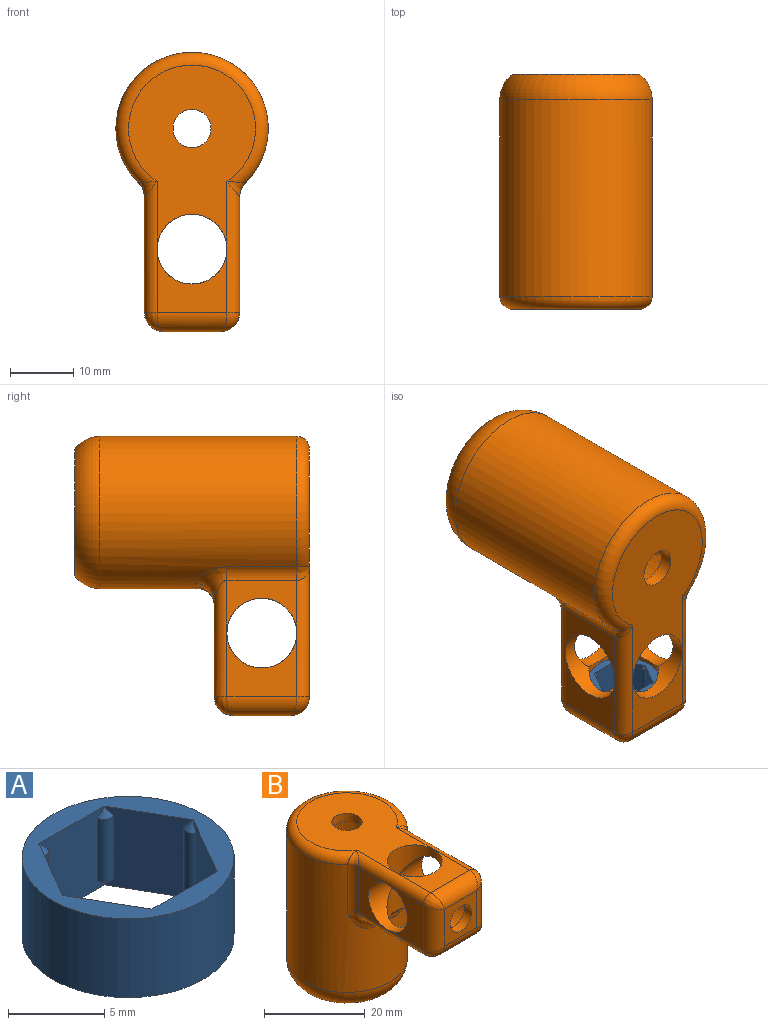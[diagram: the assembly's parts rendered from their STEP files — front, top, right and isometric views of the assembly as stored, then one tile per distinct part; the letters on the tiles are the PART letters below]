
ASSEMBLY  parts=2 mates=1
PART A: 27 faces, bbox 11x11x5 mm
  f0: plane 5x4.15mm, normal (0.87,-0.5,0), area 19.5mm2, adj f7,f8,f21,f22,f23,f24,f25,f26
  f1: plane 5x4.79mm, normal (0,-1,0), area 19.5mm2, adj f7,f8,f9,f10,f11,f21,f22,f23
  f2: plane 5x4.15mm, normal (-0.87,-0.5,0), area 19.5mm2, adj f7,f8,f9,f10,f11,f15,f16,f17
  f3: plane 5x4.15mm, normal (-0.87,0.5,0), area 19.5mm2, adj f7,f8,f12,f13,f14,f15,f16,f17
  f4: plane 5x4.79mm, normal (0,1,0), area 19.5mm2, adj f7,f8,f12,f13,f14,f18,f19,f20
  f5: plane 5x4.15mm, normal (0.87,0.5,0), area 19.5mm2, adj f7,f8,f18,f19,f20,f24,f25,f26
  f6: cylinder r=5.5mm len=11mm, axis (0,0,-1), area 172.8mm2, adj f7,f8
  f7: plane 11x11mm, normal (0,0,1), area 35.4mm2, adj f0,f1,f2,f3,f4,f5,f6
  f8: plane 11x11mm, normal (0,0,-1), area 35.4mm2, adj f0,f1,f2,f3,f4,f5,f6
  f9: cylinder r=0.5mm len=4mm, axis (0,0,-1), area 4.2mm2, adj f1,f2,f10,f11
  f10: cone r=0.5mm half-angle=45deg, axis (0,0,-1), area 0.4mm2, adj f1,f2,f9
  f11: cone r=0.5mm half-angle=45deg, axis (0,0,1), area 0.4mm2, adj f1,f2,f9
  f12: cylinder r=0.5mm len=4mm, axis (0,0,-1), area 4.2mm2, adj f3,f4,f13,f14
  f13: cone r=0.5mm half-angle=45deg, axis (0,0,-1), area 0.4mm2, adj f3,f4,f12
  f14: cone r=0.5mm half-angle=45deg, axis (0,0,1), area 0.4mm2, adj f3,f4,f12
  f15: cylinder r=0.5mm len=4mm, axis (0,0,-1), area 4.2mm2, adj f2,f3,f16,f17
  f16: cone r=0.5mm half-angle=45deg, axis (0,0,-1), area 0.4mm2, adj f2,f3,f15
  f17: cone r=0.5mm half-angle=45deg, axis (0,0,1), area 0.4mm2, adj f2,f3,f15
  f18: cylinder r=0.5mm len=4mm, axis (0,0,-1), area 4.2mm2, adj f4,f5,f19,f20
  f19: cone r=0.5mm half-angle=45deg, axis (0,0,-1), area 0.4mm2, adj f4,f5,f18
  f20: cone r=0.5mm half-angle=45deg, axis (0,0,1), area 0.4mm2, adj f4,f5,f18
  f21: cylinder r=0.5mm len=4mm, axis (0,0,-1), area 4.2mm2, adj f0,f1,f22,f23
  f22: cone r=0.5mm half-angle=45deg, axis (0,0,-1), area 0.4mm2, adj f0,f1,f21
  f23: cone r=0.5mm half-angle=45deg, axis (0,0,1), area 0.4mm2, adj f0,f1,f21
  f24: cylinder r=0.5mm len=4mm, axis (0,0,-1), area 4.2mm2, adj f0,f5,f25,f26
  f25: cone r=0.5mm half-angle=45deg, axis (0,0,-1), area 0.4mm2, adj f0,f5,f24
  f26: cone r=0.5mm half-angle=45deg, axis (0,0,1), area 0.4mm2, adj f0,f5,f24
PART B: 56 faces, bbox 26x45x38 mm
  f0: plane 5.04x2.17mm, normal (0,0,-1), area 3.5mm2, adj f27,f38,f52
  f1: plane 5.04x2.17mm, normal (0,0,-1), area 3.5mm2, adj f27,f37,f50
  f2: plane 11x10mm, normal (-1,0,0), area 62.5mm2, adj f28,f34,f38,f43
  f3: plane 11x10mm, normal (0,0,1), area 62.5mm2, adj f22,f34,f36,f39
  f4: plane 11x8.29mm, normal (1,0,0), area 43.6mm2, adj f29,f36,f37,f48
  f5: cylinder r=10mm len=35mm, axis (0,0,-1), area 2077.9mm2, adj f7,f8,f11,f13,f14,f16,f19,f33
  f6: cylinder r=12mm len=31mm, axis (0,0,-1), area 2050.7mm2, adj f33,f35,f48,f49,f50,f51,f52,f53
  f7: plane 6.5x5mm, normal (0,0,-1), area 26.1mm2, adj f5,f14,f15,f16,f17
  f8: plane 20x19.37mm, normal (0,0,-1), area 227.3mm2, adj f5,f9,f11,f12,f13,f14,f15,f16
  f9: cylinder r=3mm len=6mm, axis (0,0,-1), area 37.7mm2, adj f8,f10
  f10: plane 29x20mm, normal (0,0,1), area 343.2mm2, adj f9,f22,f34,f35,f36
  f11: plane 12x3.68mm, normal (0,1,0), area 44.2mm2, adj f5,f8,f12,f19
  f12: cylinder r=2.5mm len=12mm, axis (0,0,-1), area 95.5mm2, adj f8,f11,f13,f19
  f13: plane 12x3.58mm, normal (0,-1,0), area 42.9mm2, adj f5,f8,f12,f19
  f14: plane 12x3.58mm, normal (0,-1,0), area 42.9mm2, adj f5,f7,f8,f15
  f15: cylinder r=2.5mm len=12mm, axis (0,0,-1), area 95.5mm2, adj f7,f8,f14,f16
  f16: plane 12x3.68mm, normal (0,1,0), area 44.2mm2, adj f5,f7,f8,f15
  f17: cylinder r=1mm len=12mm, axis (0,0,-1), area 75.4mm2, adj f7,f21
  f18: cylinder r=1mm len=12mm, axis (0,0,-1), area 75.4mm2, adj f19,f20
  f19: plane 6.5x5mm, normal (0,0,-1), area 26.1mm2, adj f5,f11,f12,f13,f18
  f20: plane 2x2mm, normal (0,0,-1), area 3.1mm2, adj f18
  f21: plane 2x2mm, normal (0,0,-1), area 3.1mm2, adj f17
  f22: cylinder r=5.5mm len=11mm, axis (0,0,1), area 114.2mm2, adj f3,f10,f28,f29,f30
  f23: plane 11x10mm, normal (0,0,-1), area 62.5mm2, adj f27,f37,f38,f46
  f24: plane 11x10mm, normal (1,0,0), area 62.5mm2, adj f29,f36,f37,f42
  f25: plane 11x8.29mm, normal (-1,0,0), area 43.6mm2, adj f28,f34,f38,f54
  f26: plane 9x9mm, normal (0,-1,0), area 52.7mm2, adj f32,f39,f42,f43,f46
  f27: cylinder r=5.5mm len=11mm, axis (0,0,1), area 116.5mm2, adj f0,f1,f23,f28,f29,f30,f51
  f28: cylinder r=5.5mm len=11mm, axis (-1,0,0), area 113.1mm2, adj f2,f22,f25,f27,f30
  f29: cylinder r=5.5mm len=11mm, axis (-1,0,0), area 115.3mm2, adj f4,f22,f24,f27,f30
  f30: cylinder r=5.5mm len=11mm, axis (0,-1,0), area 211.2mm2, adj f22,f27,f28,f29,f31
  f31: plane 11x11mm, normal (0,1,0), area 66.8mm2, adj f30,f32
  f32: cylinder r=3mm len=6mm, axis (0,1,0), area 37.7mm2, adj f26,f31
  f33: torus R=7mm, axis (0,0,-1), area 329.6mm2, adj f5,f6
  f34: cylinder r=2mm len=20.65mm, axis (0,-1,0), area 60mm2, adj f2,f3,f10,f25,f41,f55
  f35: torus R=10mm, axis (0,0,1), area 171.8mm2, adj f6,f10,f47,f55
  f36: cylinder r=2mm len=20.65mm, axis (0,1,0), area 60mm2, adj f3,f4,f10,f24,f40,f47
  f37: cylinder r=2mm len=18.29mm, axis (0,-1,0), area 52.4mm2, adj f1,f4,f23,f24,f44,f49
  f38: cylinder r=2mm len=18.29mm, axis (0,1,0), area 52.4mm2, adj f0,f2,f23,f25,f45,f53
  f39: cylinder r=3mm len=11mm, axis (1,0,0), area 47.1mm2, adj f3,f26,f40,f41
  f40: bspline ~3.65x3mm, area 9.7mm2, adj f36,f39,f42
  f41: bspline ~3.16x3mm, area 9.7mm2, adj f34,f39,f43
  f42: cylinder r=3mm len=11mm, axis (0,0,1), area 47.1mm2, adj f24,f26,f40,f44
  f43: cylinder r=3mm len=11mm, axis (0,0,-1), area 47.1mm2, adj f2,f26,f41,f45
  f44: bspline ~3.16x3mm, area 9.7mm2, adj f37,f42,f46
  f45: bspline ~3.65x3mm, area 9.7mm2, adj f38,f43,f46
  f46: cylinder r=3mm len=11mm, axis (-1,0,0), area 47.1mm2, adj f23,f26,f44,f45
  f47: bspline ~2.9x2.36mm, area 3.2mm2, adj f35,f36,f48
  f48: cylinder r=3mm len=11mm, axis (0,0,-1), area 26.2mm2, adj f4,f6,f47,f49
  f49: bspline ~5.92x5.76mm, area 18.9mm2, adj f6,f37,f48,f50
  f50: torus R=15mm, axis (0,0,1), area 9.3mm2, adj f1,f6,f49,f51
  f51: bspline ~6.67x3mm, area 20.9mm2, adj f6,f27,f50,f52
  f52: torus R=15mm, axis (0,0,1), area 9.3mm2, adj f0,f6,f51,f53
  f53: bspline ~5.92x5.76mm, area 18.9mm2, adj f6,f38,f52,f54
  f54: cylinder r=3mm len=11mm, axis (0,0,-1), area 26.2mm2, adj f6,f25,f53,f55
  f55: bspline ~2.9x2.36mm, area 3.2mm2, adj f34,f35,f54
PLACE A t=(-1.99,-24.91,-2.66)mm
PLACE B rot(axis=(1,0,0),90deg) t=(-1.99,4.59,27.34)mm
MATE fastened B.f30 <-> A.f6  axis (0,0,1) through (-1.99,-24.91,-2.66)mm
